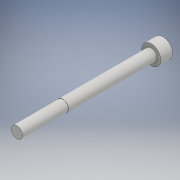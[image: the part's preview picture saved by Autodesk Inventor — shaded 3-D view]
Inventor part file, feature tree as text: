
AUTODESK INVENTOR PART (.ipt)
format: ipt  version: 2018 (Build 220112000, 112)  size: 110,080 bytes
history: native  units: mm
features: extrude x3, sketch x3
ambient origin geometry x8: Origin, YZ Plane, XZ Plane, XY Plane, X Axis, Y Axis, Z Axis, Center Point
bodies: Solid1 (feature_tree)
feature tree (6):
  extrude  "Extrusion1"  Depth=7.92mm TaperAngle=0.0deg
  extrude  "Extrusion2"  Depth=98.1mm TaperAngle=0.0deg
  extrude  "Extrusion3"  Depth=30.75mm TaperAngle=0.0deg
  sketch  "Sketch1"  dims[d0=12.82mm d1=7.92mm d2=0.0mm]
  sketch  "Sketch2"  dims[d3=7.81mm d4=98.1mm d5=0.0mm]
  sketch  "Sketch3"  dims[d6=0.1mm d7=30.75mm d8=0.0mm]
